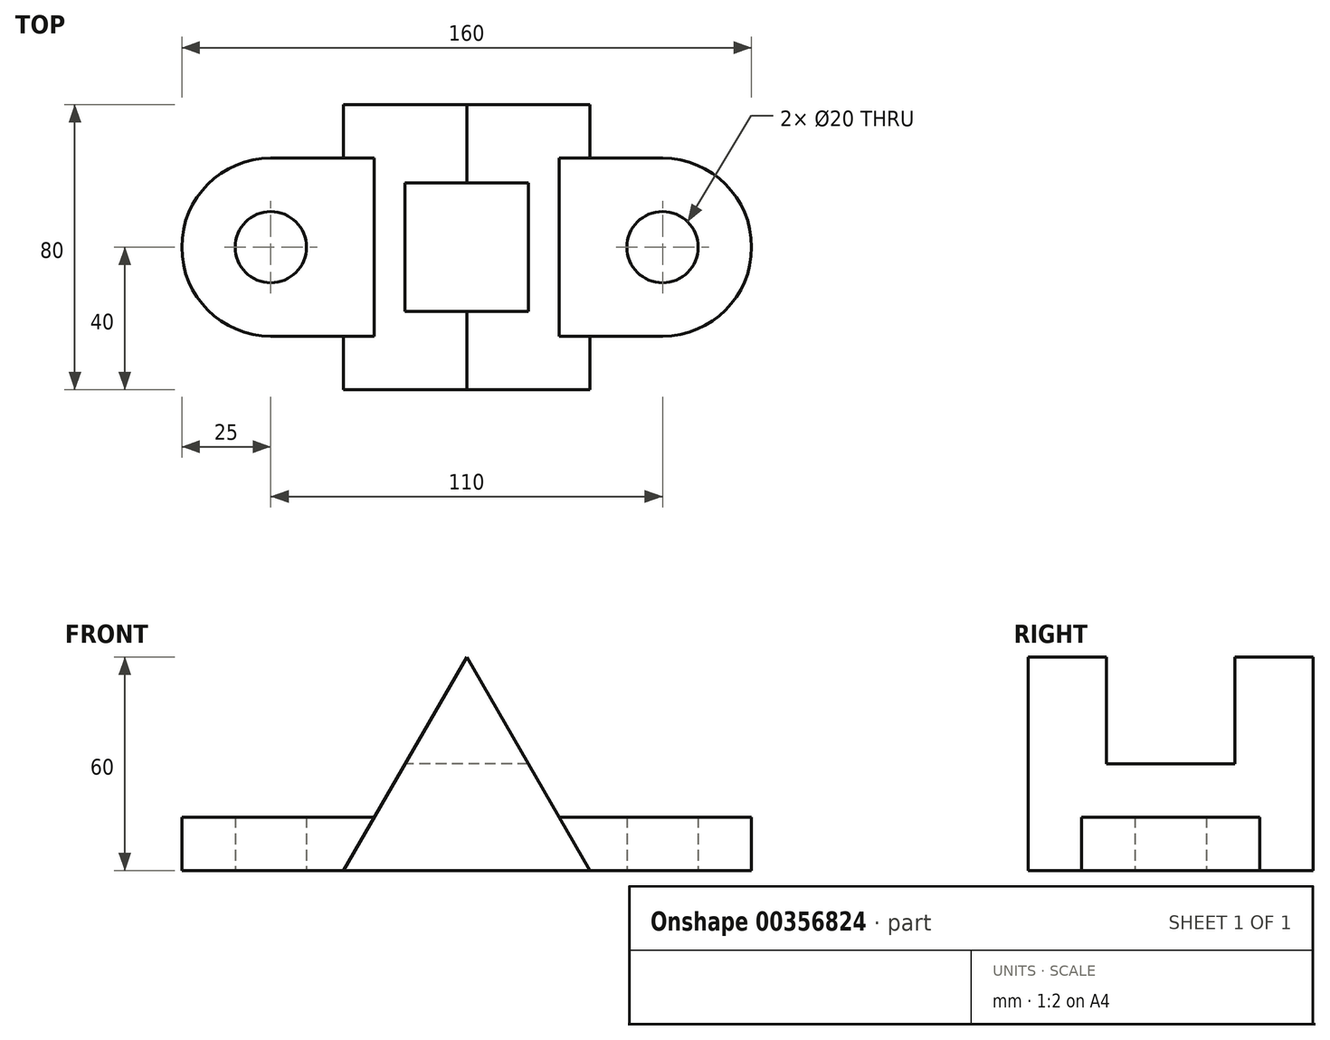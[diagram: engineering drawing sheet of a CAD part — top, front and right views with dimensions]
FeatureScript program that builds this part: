
annotation { "Feature Type Name" : "Feature", "Feature Type Description" : "" }
export const myFeature = defineFeature(function(context is Context, id is Id, definition is map)
    precondition{}
    {
        {
            var Q0;
            Q0=qCreatedBy(makeId("Top.planeOp"),FACE);
            var sketch = newSketch(context, id + "F0", { "sketchPlane" : qUnion([Q0])});
            skArc(sketch, "E0", {"start": v(55, -25) * mm, "mid": v(80, 0) * mm, "end": v(55, 25) * mm});
            skCircle(sketch, "E1", {"center": v(55, 0) * mm, "radius": 10 * mm});
            skArc(sketch, "E2.MirrorC", {"start": v(-55, -25) * mm, "mid": v(-80, 0) * mm, "end": v(-55, 25) * mm});
            skCircle(sketch, "E3.MirrorC", {"center": v(-55, 0) * mm, "radius": 10 * mm});
            skLineSegment(sketch, "E4", {"start": v(-55, 25) * mm, "end": v(55, 25) * mm});
            skLineSegment(sketch, "E5.MirrorCS", {"start": v(-55, -25) * mm, "end": v(55, -25) * mm});
            skSolve(sketch);
        }
        {
            var Q0;
            Q0 = qSketchRegion(id + "F0", true);
            extrude(context, id + "F1", {"entities" : qUnion([Q0]), "depth" : 15 * mm});
        }
        {
            var Q0;
            Q0=qCreatedBy(makeId("Front.planeOp"),FACE);
            var sketch = newSketch(context, id + "F2", { "sketchPlane" : qUnion([Q0])});
            skLineSegment(sketch, "E6", {"start": v(0, 60) * mm, "end": v(-34.64, 0) * mm});
            skLineSegment(sketch, "E7.MirrorCS", {"start": v(0, 60) * mm, "end": v(34.64, 0) * mm});
            skLineSegment(sketch, "E8", {"start": v(-34.64, 0) * mm, "end": v(34.64, 0) * mm});
            skSolve(sketch);
        }
        {
            var Q0;
            Q0 = qSketchRegion(id + "F2", true);
            extrude(context, id + "F3", {"entities" : qUnion([Q0]), "operationType" : NewBodyOperationType.ADD, "depth" : 40 * mm});
        }
        {
            var Q0;
            Q0=makeQuery(id+"F3.opExtrude","CAP_FACE",FACE,{"disambiguationData":[OSD([sQuery(id+"F2.wireOp",EDGE,"E6"),sQuery(id+"F2.wireOp",EDGE,"E7.MirrorCS"),sQuery(id+"F2.wireOp",EDGE,"E8")])],"isStart":false});
            extrude(context, id + "F4", {"entities" : qUnion([Q0]), "operationType" : NewBodyOperationType.ADD, "depth" : -80 * mm});
        }
        {
            var Q0;
            Q0=qCreatedBy(makeId("Right.planeOp"),FACE);
            var sketch = newSketch(context, id + "F5", { "sketchPlane" : qUnion([Q0])});
            skLineSegment(sketch, "E9.bottom", {"start": v(-18, 60.55) * mm, "end": v(18, 60.55) * mm});
            skLineSegment(sketch, "E9.top", {"start": v(-18, 30) * mm, "end": v(18, 30) * mm});
            skLineSegment(sketch, "E9.left", {"start": v(-18, 60.55) * mm, "end": v(-18, 30) * mm});
            skLineSegment(sketch, "E9.right", {"start": v(18, 60.55) * mm, "end": v(18, 30) * mm});
            skSolve(sketch);
        }
        {
            var Q0;
            Q0 = qSketchRegion(id + "F5", true);
            extrude(context, id + "F6", {"entities" : qUnion([Q0]), "operationType" : NewBodyOperationType.REMOVE, "depth" : 25 * mm});
        }
        {
            var Q0;
            Q0=makeQuery(id+"F6.boolean.opBoolean","COPY",FACE,{"derivedFrom":makeQuery(id+"F6.opExtrude","CAP_FACE",FACE,{"disambiguationData":[OSD([sQuery(id+"F5.wireOp",EDGE,"E9.bottom"),sQuery(id+"F5.wireOp",EDGE,"E9.top"),sQuery(id+"F5.wireOp",EDGE,"E9.left"),sQuery(id+"F5.wireOp",EDGE,"E9.right")])],"isStart":true})});
            extrude(context, id + "F7", {"entities" : qUnion([Q0]), "operationType" : NewBodyOperationType.REMOVE, "oppositeDirection" : true, "depth" : 25 * mm});
        }
    });
